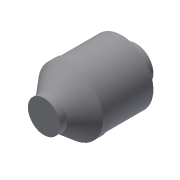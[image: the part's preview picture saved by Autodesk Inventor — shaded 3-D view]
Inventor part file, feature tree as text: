
AUTODESK INVENTOR PART (.ipt)
format: ipt  version: 2019.4 (Build 234330000, 330)  size: 104,448 bytes
history: native  units: mm
features: revolve x1, sketch x1
ambient origin geometry x8: Origin, YZ Plane, XZ Plane, XY Plane, X Axis, Y Axis, Z Axis, Center Point
bodies: Solid1 (feature_tree)
feature tree (2):
  revolve  "Revolution1"  [1 undecoded]
  sketch  "Sketch1"  dims[d0=7.78mm d1=6.36mm d2=41.4mm d3=7.21mm d4=14.5mm d5=90.0deg]
note: 1 required parameter value undecoded (feature->parameter linkage not recoverable at this tier; creation-order binding heuristic only, values carry confidence <= 0.55)
